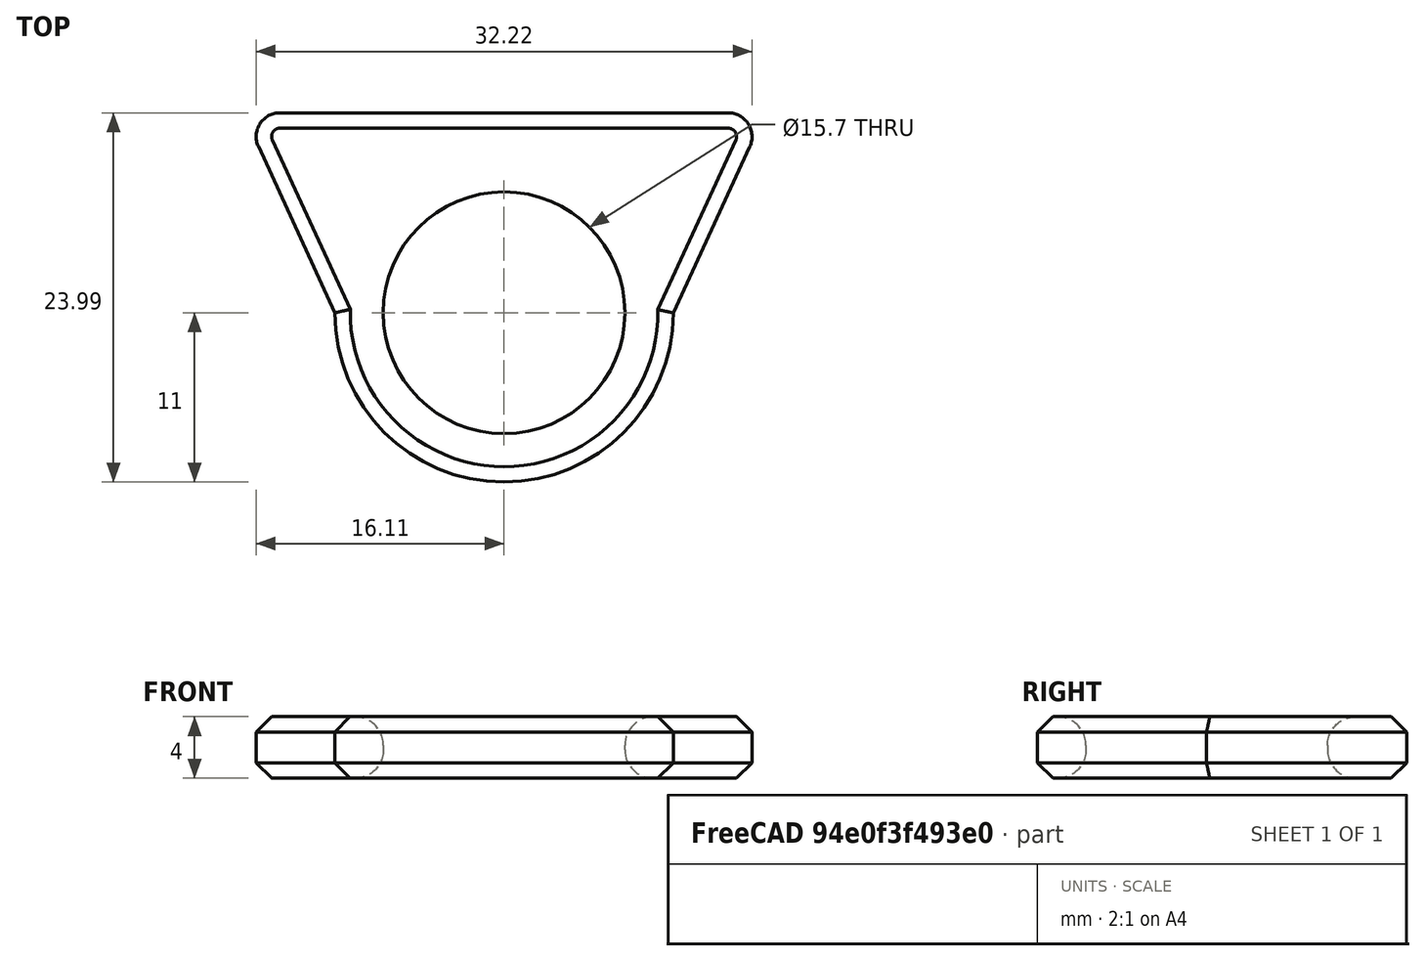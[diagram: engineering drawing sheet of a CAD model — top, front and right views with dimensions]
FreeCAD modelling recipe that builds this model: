
FCSTD DOCUMENT  (FreeCAD 0.18R16117 (Git))
Label: CB.EN.U4AIE19002
License: All rights reserved
LicenseURL: http://en.wikipedia.org/wiki/All_rights_reserved
objects: Sketcher::SketchObject×1, PartDesign::Pad×1, PartDesign::Fillet×1, PartDesign::Chamfer×1, PartDesign::Body×1, Part::Part2DObjectPython×1
note: 7 computed .brp shape members not serialized (recipe doc carries the construction recipe); baked Part::Feature solids carry a one-line shape summary decoded from their .brp

FEATURE [Sketcher::SketchObject] Sketch
  MapMode = 5
  Support = -> [XY_Plane]
  sketch-geometry (7):
    g0: Circle CenterX=0 CenterY=0 CenterZ=0 NormalX=0 NormalY=0 NormalZ=1 AngleXU=0 Radius=7.85
    g1: ArcOfCircle CenterX=-0.00160687 CenterY=0 CenterZ=0 NormalX=0 NormalY=0 NormalZ=1 AngleXU=0 Radius=11 StartAngle=3.14159 EndAngle=6.28183
    g2: LineSegment StartX=-11.0016 StartY=1.3e-15 StartZ=0 EndX=-15.9691 EndY=10.8033 EndZ=0
    g3: LineSegment StartX=-14.5672 StartY=12.9909 StartZ=0 EndX=14.5649 EndY=12.9909 EndZ=0
    g4: LineSegment StartX=15.9686 StartY=10.801 StartZ=0 EndX=10.9984 EndY=-0.014925 EndZ=0
    g5: ArcOfCircle CenterX=14.5649 CenterY=11.446 CenterZ=0 NormalX=0 NormalY=0 NormalZ=1 AngleXU=0 Radius=1.54484 StartAngle=5.85243 EndAngle=7.85398
    g6: ArcOfCircle CenterX=-14.5672 CenterY=11.4479 CenterZ=0 NormalX=0 NormalY=0 NormalZ=1 AngleXU=0 Radius=1.54295 StartAngle=1.5708 EndAngle=3.57257
  constraints (8):
    c: Radius(g1) = 11
    c: Radius(g0) = 7.85
    c: Coincident(g1,g2)
    c: Coincident(g1,g4)
    c: Tangent(g3,g5) = 1.5708
    c: Tangent(g4,g5) = 1.5708
    c: Tangent(g2,g6) = 1.5708
    c: Tangent(g3,g6) = 1.5708
FEATURE [PartDesign::Pad] Pad
  Length = 4
  Length2 = 100
  Profile = -> Sketch
  Type = 0
FEATURE [PartDesign::Fillet] Fillet
  Base = -> Pad [Edge21,Edge20]
  BaseFeature = -> Pad
  Radius = 1.85
FEATURE [PartDesign::Chamfer] Chamfer
  Base = -> Fillet [Edge24,Edge17,Edge18,Edge19,Edge14,Edge15,Edge16,Edge7,Edge10,Edge11,Edge12,Edge13,Edge9]
  BaseFeature = -> Fillet
  Size = 1
FEATURE [PartDesign::Body] Body
  Group = -> [Sketch,Pad,Fillet,Chamfer]
  Origin = -> Origin
  Tip = -> Chamfer
FEATURE [Part::Part2DObjectPython] ShapeString  # Draft 2D object (typed FeaturePython)
  FontFile = <path>
  Placement = pos=(-9.77,7.75,4) rot=(0,0,1;0rad)
  Size = 2.5
  String = AP
  Tracking = 0
note: 1 file-system path scrubbed to <path> (originals preserved in the JSON sidecar)
